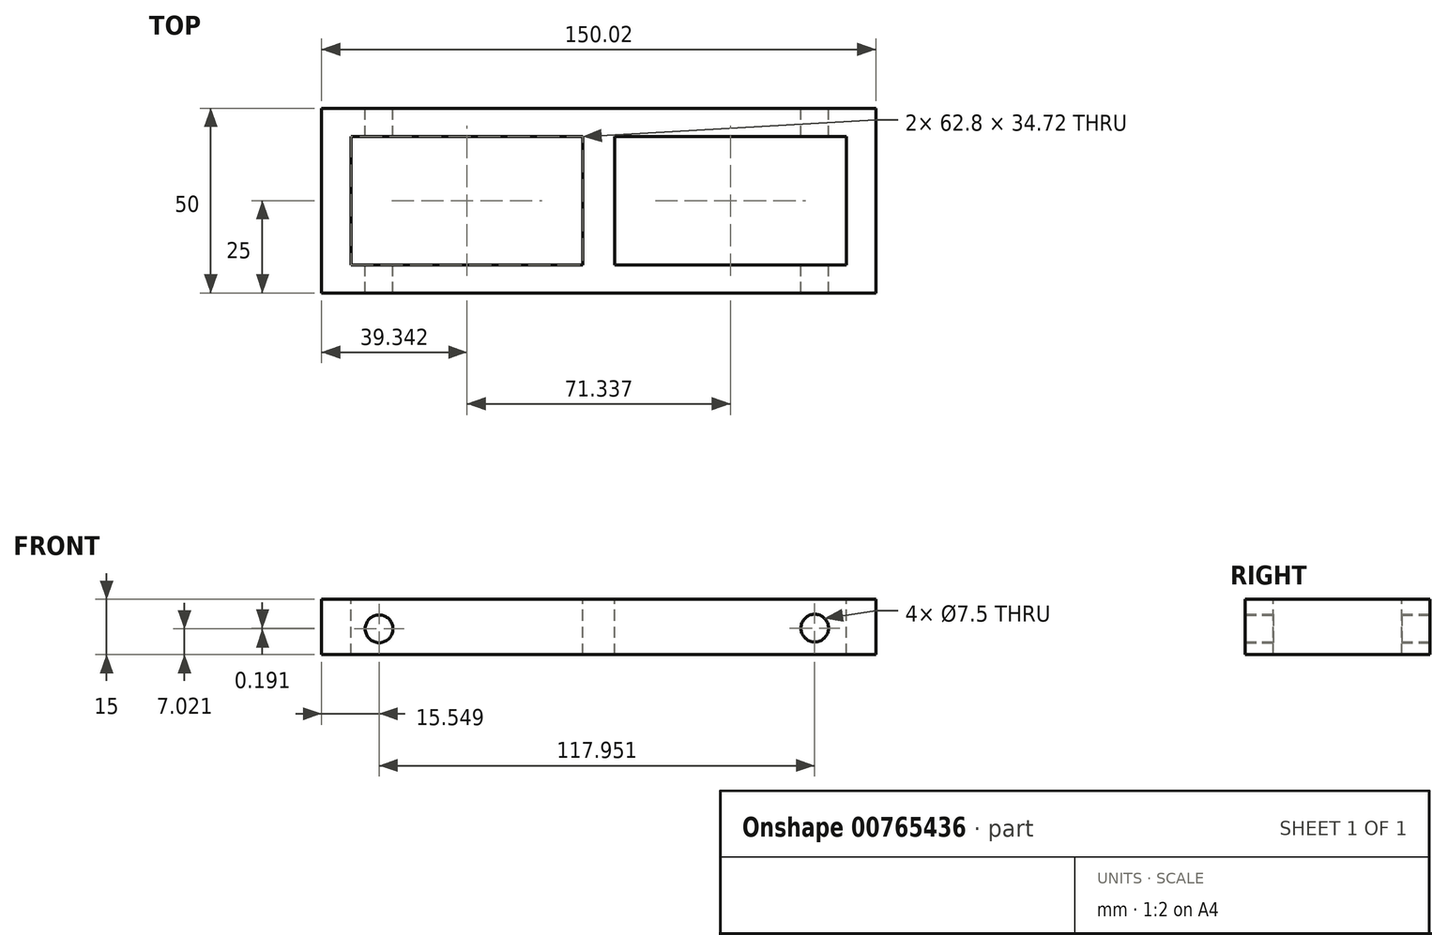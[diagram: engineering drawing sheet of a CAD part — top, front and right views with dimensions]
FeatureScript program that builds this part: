
annotation { "Feature Type Name" : "Feature", "Feature Type Description" : "" }
export const myFeature = defineFeature(function(context is Context, id is Id, definition is map)
    precondition{}
    {
        {
            var Q0;
            Q0=qCreatedBy(makeId("Top.planeOp"),FACE);
            var sketch = newSketch(context, id + "F0", { "sketchPlane" : qUnion([Q0])});
            skLineSegment(sketch, "E0.bottom", {"start": v(75, 25) * mm, "end": v(-75, 25) * mm});
            skLineSegment(sketch, "E0.top", {"start": v(75, -25) * mm, "end": v(-75, -25) * mm});
            skLineSegment(sketch, "E0.left", {"start": v(75, 25) * mm, "end": v(75, -25) * mm});
            skLineSegment(sketch, "E0.right", {"start": v(-75, 25) * mm, "end": v(-75, -25) * mm});
            skPoint(sketch, "E0.middle", {"position": v(0, 0) * mm});
            skSolve(sketch);
        }
        {
            var Q0;
            Q0=makeQuery(id+"F0.imprint","IMPRINT",FACE,{"disambiguationData":[TD([[makeQuery(id+"F0.imprint","IMPRINT",EDGE,{"derivedFrom":sQuery(id+"F0.wireOp",EDGE,"E0.bottom")}),1.0]])]});
            extrude(context, id + "F1", {"entities" : qUnion([Q0]), "depth" : 15 * mm, "offsetDistance" : 25 * mm});
        }
        {
            var Q0;
            Q0=makeQuery(id+"F1.opExtrude","CAP_FACE",FACE,{"disambiguationData":[OSD([sQuery(id+"F0.wireOp",EDGE,"E0.bottom"),sQuery(id+"F0.wireOp",EDGE,"E0.top"),sQuery(id+"F0.wireOp",EDGE,"E0.left"),sQuery(id+"F0.wireOp",EDGE,"E0.right")])],"isStart":false});
            var sketch = newSketch(context, id + "F2", { "sketchPlane" : qUnion([Q0])});
            skLineSegment(sketch, "E1.bottom", {"start": v(67.07, 17.36) * mm, "end": v(-67.07, 17.36) * mm});
            skLineSegment(sketch, "E1.top", {"start": v(67.07, -17.36) * mm, "end": v(-67.07, -17.36) * mm});
            skLineSegment(sketch, "E1.left", {"start": v(67.07, 17.36) * mm, "end": v(67.07, -17.36) * mm});
            skLineSegment(sketch, "E1.right", {"start": v(-67.07, 17.36) * mm, "end": v(-67.07, -17.36) * mm});
            skPoint(sketch, "E1.middle", {"position": v(0, 0) * mm});
            skSolve(sketch);
        }
        {
            var Q0;
            Q0=makeQuery(id+"F2.imprint","IMPRINT",FACE,{"disambiguationData":[TD([[makeQuery(id+"F2.imprint","IMPRINT",EDGE,{"derivedFrom":sQuery(id+"F2.wireOp",EDGE,"E1.bottom")}),1.0]])]});
            var sketch = newSketch(context, id + "F3", { "sketchPlane" : qUnion([Q0])});
            skSolve(sketch);
        }
        {
            var Q0;
            Q0=makeQuery(id+"F3.imprint","IMPRINT",FACE,{"disambiguationData":[TD([[makeQuery(id+"F3.imprint","IMPRINT",EDGE,{"derivedFrom":makeQuery(id+"F2.imprint","IMPRINT",EDGE,{"derivedFrom":sQuery(id+"F2.wireOp",EDGE,"E1.bottom")})}),1.0]])]});
            var sketch = newSketch(context, id + "F4", { "sketchPlane" : qUnion([Q0])});
            skSolve(sketch);
        }
        {
            var Q0;
            Q0=makeQuery(id+"F4.imprint","IMPRINT",FACE,{"disambiguationData":[TD([[makeQuery(id+"F4.imprint","IMPRINT",EDGE,{"derivedFrom":makeQuery(id+"F3.imprint","IMPRINT",EDGE,{"derivedFrom":makeQuery(id+"F2.imprint","IMPRINT",EDGE,{"derivedFrom":sQuery(id+"F2.wireOp",EDGE,"E1.bottom")})})}),1.0]])]});
            var Q1;
            Q1 = qSketchRegion(id + "F4", true);
            extrude(context, id + "F5", {"entities" : qUnion([Q0, Q1]), "operationType" : NewBodyOperationType.REMOVE, "oppositeDirection" : true, "depth" : 39.6 * mm, "offsetDistance" : 25 * mm});
        }
        {
            var Q0;
            Q0=makeQuery(id+"F2.imprint","IMPRINT",FACE,{"disambiguationData":[TD([[makeQuery(id+"F2.imprint","IMPRINT",EDGE,{"derivedFrom":sQuery(id+"F2.wireOp",EDGE,"E1.bottom")}),-1.0]])]});
            var sketch = newSketch(context, id + "F6", { "sketchPlane" : qUnion([Q0])});
            skLineSegment(sketch, "E2.bottom", {"start": v(-4.27, 20.61) * mm, "end": v(4.27, 20.61) * mm});
            skLineSegment(sketch, "E2.top", {"start": v(-4.27, -20.61) * mm, "end": v(4.27, -20.61) * mm});
            skLineSegment(sketch, "E2.left", {"start": v(-4.27, 20.61) * mm, "end": v(-4.27, -20.61) * mm});
            skLineSegment(sketch, "E2.right", {"start": v(4.27, 20.61) * mm, "end": v(4.27, -20.61) * mm});
            skPoint(sketch, "E2.middle", {"position": v(0, 0) * mm});
            skSolve(sketch);
        }
        {
            var Q0;
            {var subQ0=sQuery(id+"F6.wireOp",EDGE,"E2.left");var subQ1=makeQuery(id+"F2.imprint","IMPRINT",EDGE,{"derivedFrom":sQuery(id+"F2.wireOp",EDGE,"E1.bottom")});var subQ2=makeQuery(id+"F6.imprint","INTERSECT",VERTEX,{"derivedFrom":[subQ1,subQ0]});Q0=makeQuery(id+"F6.imprint","IMPRINT",FACE,{"disambiguationData":[TD([[makeQuery(id+"F6.imprint","IMPRINT",EDGE,{"disambiguationData":[TD([[subQ2,-1.0]])],"derivedFrom":subQ0}),1.0]])]});}
            extrude(context, id + "F7", {"entities" : qUnion([Q0]), "operationType" : NewBodyOperationType.ADD, "oppositeDirection" : true, "depth" : 15 * mm, "offsetDistance" : 25 * mm});
        }
        {
            var Q0;
            Q0=makeQuery(id+"F1.opExtrude","SWEPT_FACE",FACE,{"disambiguationData":[OSD([sQuery(id+"F0.wireOp",EDGE,"E0.bottom")])]});
            var sketch = newSketch(context, id + "F8", { "sketchPlane" : qUnion([Q0])});
            skPoint(sketch, "E3", {"position": v(-58.5, 7.21) * mm});
            skPoint(sketch, "E4", {"position": v(59.18, 7.21) * mm});
            skSolve(sketch);
        }
        {
            var Q0;
            Q0=sQuery(id+"F8.wireOp",VERTEX,"E3");
            var Q1;
            Q1=makeQuery(id+"F1.opExtrude","SWEPT_BODY",BODY,{"disambiguationData":[OSD([sQuery(id+"F0.wireOp",EDGE,"E0.bottom"),sQuery(id+"F0.wireOp",EDGE,"E0.top"),sQuery(id+"F0.wireOp",EDGE,"E0.left"),sQuery(id+"F0.wireOp",EDGE,"E0.right")])]});
            hole(context, id + "F9", {"style" : HoleStyle.SIMPLE, "endStyle" : HoleEndStyle.THROUGH, "holeDiameter" : 7.5 * mm, "majorDiameter" : 5 * mm, "isTappedThrough" : true, "tappedDepth" : 12 * mm, "tapClearance" : 3, "locations" : qUnion([Q0]), "scope" : qUnion([Q1])});
        }
        {
            var Q0;
            Q0=makeQuery(id+"F1.opExtrude","SWEPT_FACE",FACE,{"disambiguationData":[OSD([sQuery(id+"F0.wireOp",EDGE,"E0.bottom")])]});
            var sketch = newSketch(context, id + "F10", { "sketchPlane" : qUnion([Q0])});
            skPoint(sketch, "E5", {"position": v(59.46, 7.02) * mm});
            skSolve(sketch);
        }
        {
            var Q0;
            Q0=sQuery(id+"F10.wireOp",VERTEX,"E5");
            var Q1;
            Q1=makeQuery(id+"F1.opExtrude","SWEPT_BODY",BODY,{"disambiguationData":[OSD([sQuery(id+"F0.wireOp",EDGE,"E0.bottom"),sQuery(id+"F0.wireOp",EDGE,"E0.top"),sQuery(id+"F0.wireOp",EDGE,"E0.left"),sQuery(id+"F0.wireOp",EDGE,"E0.right")])]});
            hole(context, id + "F11", {"style" : HoleStyle.SIMPLE, "endStyle" : HoleEndStyle.THROUGH, "holeDiameter" : 7.5 * mm, "majorDiameter" : 5 * mm, "isTappedThrough" : true, "tappedDepth" : 12 * mm, "tapClearance" : 3, "locations" : qUnion([Q0]), "scope" : qUnion([Q1])});
        }
    });
